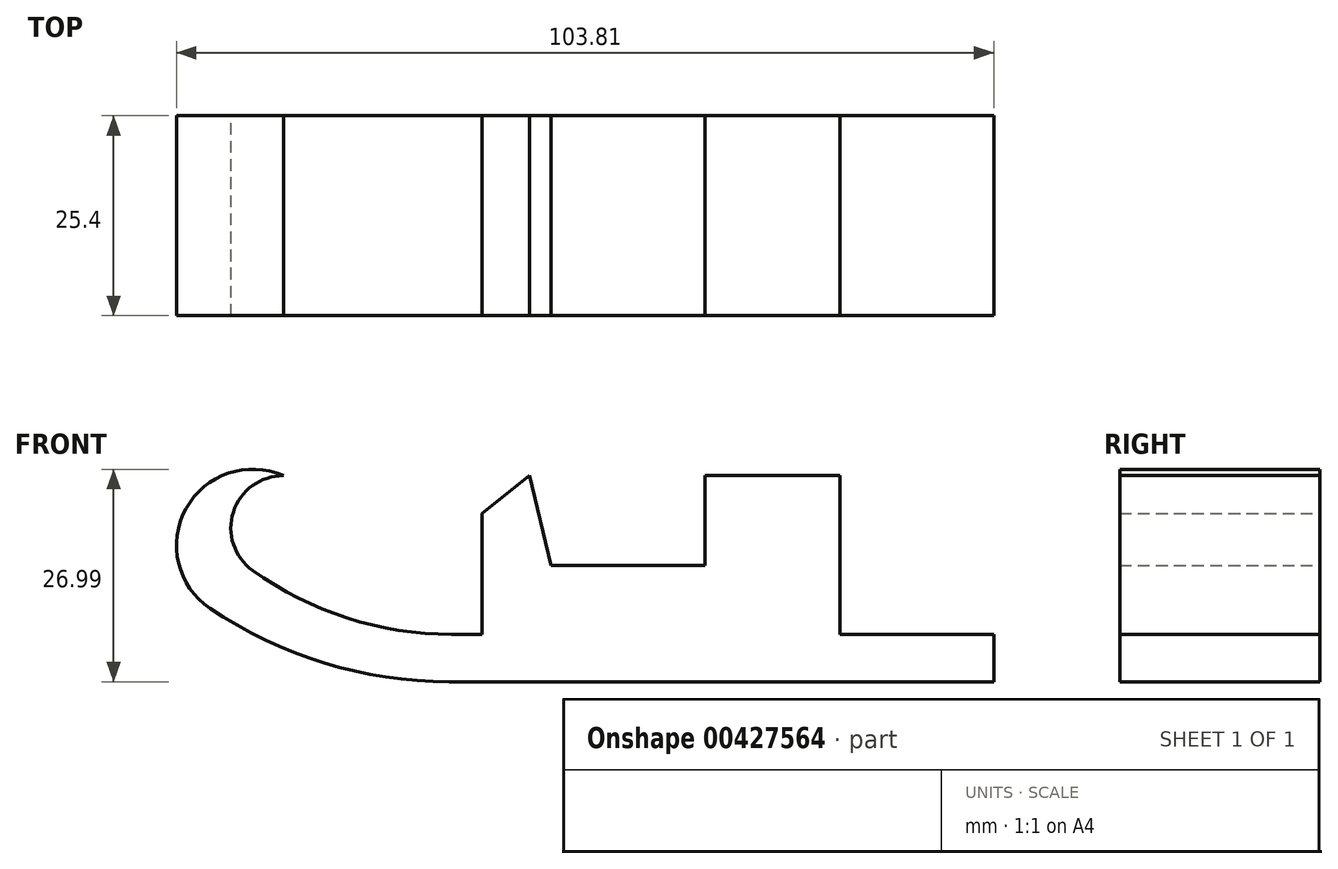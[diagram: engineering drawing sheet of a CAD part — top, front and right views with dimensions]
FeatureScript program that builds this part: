
annotation { "Feature Type Name" : "Feature", "Feature Type Description" : "" }
export const myFeature = defineFeature(function(context is Context, id is Id, definition is map)
    precondition{}
    {
        {
            var Q0;
            Q0=qCreatedBy(makeId("Front.planeOp"),FACE);
            var sketch = newSketch(context, id + "F0", { "sketchPlane" : qUnion([Q0])});
            skLineSegment(sketch, "E0", {"start": v(-24.66, -26.17) * mm, "end": v(44.52, -26.17) * mm});
            skLineSegment(sketch, "E1", {"start": v(44.52, -26.17) * mm, "end": v(44.52, -20.15) * mm});
            skLineSegment(sketch, "E2", {"start": v(44.52, -20.15) * mm, "end": v(-24.36, -20.15) * mm});
            skArc(sketch, "E3", {"start": v(-24.66, -26.17) * mm, "mid": v(-40.55, -23.79) * mm, "end": v(-55.04, -16.84) * mm});
            skArc(sketch, "E4", {"start": v(-55.04, -16.84) * mm, "mid": v(-58.08, -4.16) * mm, "end": v(-45.72, 0) * mm});
            skArc(sketch, "E5", {"start": v(-24.36, -20.15) * mm, "mid": v(-37.63, -18.07) * mm, "end": v(-49.62, -12.03) * mm});
            skArc(sketch, "E6", {"start": v(-49.62, -12.03) * mm, "mid": v(-52.07, -4.59) * mm, "end": v(-45.72, 0) * mm});
            skLineSegment(sketch, "E7", {"start": v(-20.45, -20.15) * mm, "end": v(-20.45, -4.81) * mm});
            skLineSegment(sketch, "E8", {"start": v(-20.45, -4.81) * mm, "end": v(-14.44, 0) * mm});
            skLineSegment(sketch, "E9", {"start": v(-14.44, 0) * mm, "end": v(-11.73, -11.43) * mm});
            skLineSegment(sketch, "E10", {"start": v(-11.73, -11.43) * mm, "end": v(7.82, -11.43) * mm});
            skLineSegment(sketch, "E11", {"start": v(7.82, -11.43) * mm, "end": v(7.82, 0) * mm});
            skLineSegment(sketch, "E12", {"start": v(7.82, 0) * mm, "end": v(24.97, 0) * mm});
            skLineSegment(sketch, "E13", {"start": v(24.97, 0) * mm, "end": v(24.97, -20.15) * mm});
            skSolve(sketch);
        }
        {
            var Q0;
            Q0 = qSketchRegion(id + "F0", true);
            extrude(context, id + "F1", {"entities" : qUnion([Q0]), "depth" : 25.4 * mm});
        }
    });
